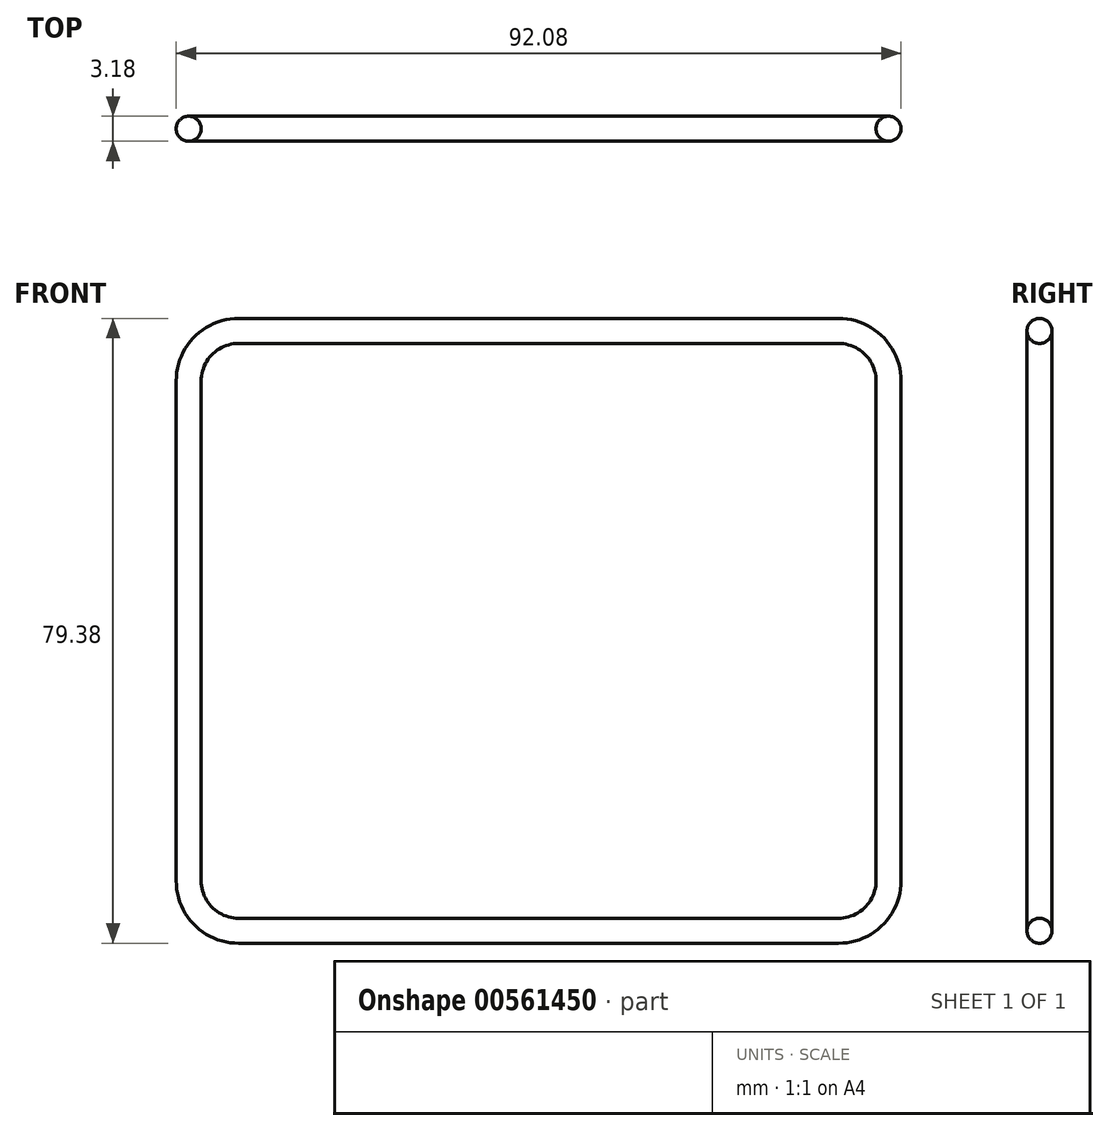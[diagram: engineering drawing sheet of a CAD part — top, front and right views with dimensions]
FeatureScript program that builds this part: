
annotation { "Feature Type Name" : "Feature", "Feature Type Description" : "" }
export const myFeature = defineFeature(function(context is Context, id is Id, definition is map)
    precondition{}
    {
        {
            var Q0;
            Q0=qCreatedBy(makeId("Front.planeOp"),FACE);
            var sketch = newSketch(context, id + "F0", { "sketchPlane" : qUnion([Q0])});
            skLineSegment(sketch, "E0.bottom", {"start": v(38.1, 38.1) * mm, "end": v(0, 38.1) * mm});
            skLineSegment(sketch, "E0.top", {"start": v(38.1, -38.1) * mm, "end": v(-38.1, -38.1) * mm});
            skLineSegment(sketch, "E0.left", {"start": v(44.45, 31.75) * mm, "end": v(44.45, -31.75) * mm});
            skLineSegment(sketch, "E0.right", {"start": v(-44.45, 31.75) * mm, "end": v(-44.45, -31.75) * mm});
            skPoint(sketch, "E0.middle", {"position": v(0, 0) * mm});
            skPoint(sketch, "E1.visualSharp", {"position": v(-44.45, 38.1) * mm});
            skArc(sketch, "E1.filletArc", {"start": v(-38.1, 38.1) * mm, "mid": v(-42.6, 36.24) * mm, "end": v(-44.45, 31.75) * mm});
            skPoint(sketch, "E2.visualSharp", {"position": v(44.45, 38.1) * mm});
            skArc(sketch, "E2.filletArc", {"start": v(44.45, 31.75) * mm, "mid": v(42.6, 36.24) * mm, "end": v(38.1, 38.1) * mm});
            skPoint(sketch, "E3.visualSharp", {"position": v(44.45, -38.1) * mm});
            skArc(sketch, "E3.filletArc", {"start": v(38.1, -38.1) * mm, "mid": v(42.6, -36.24) * mm, "end": v(44.45, -31.75) * mm});
            skPoint(sketch, "E4.visualSharp", {"position": v(-44.45, -38.1) * mm});
            skArc(sketch, "E4.filletArc", {"start": v(-44.45, -31.75) * mm, "mid": v(-42.6, -36.24) * mm, "end": v(-38.1, -38.1) * mm});
            skLineSegment(sketch, "E5", {"start": v(0, 38.1) * mm, "end": v(-38.1, 38.1) * mm});
            skSolve(sketch);
        }
        {
            var Q0;
            Q0=qCreatedBy(makeId("Right.planeOp"),FACE);
            var sketch = newSketch(context, id + "F1", { "sketchPlane" : qUnion([Q0])});
            skCircle(sketch, "E6", {"center": v(0, 38.1) * mm, "radius": 1.59 * mm});
            skSolve(sketch);
        }
        {
            var Q0;
            Q0=makeQuery(id+"F1.imprint","IMPRINT",FACE,{"disambiguationData":[TD([[makeQuery(id+"F1.imprint","IMPRINT",EDGE,{"derivedFrom":sQuery(id+"F1.wireOp",EDGE,"E6")}),1.0]])]});
            var Q1;
            Q1=sQuery(id+"F0.wireOp",EDGE,"E5");
            var Q2;
            Q2=sQuery(id+"F0.wireOp",EDGE,"E1.filletArc");
            var Q3;
            Q3=sQuery(id+"F0.wireOp",EDGE,"E0.right");
            var Q4;
            Q4=sQuery(id+"F0.wireOp",EDGE,"E4.filletArc");
            var Q5;
            Q5=sQuery(id+"F0.wireOp",EDGE,"E0.top");
            var Q6;
            Q6=sQuery(id+"F0.wireOp",EDGE,"E3.filletArc");
            var Q7;
            Q7=sQuery(id+"F0.wireOp",EDGE,"E0.left");
            var Q8;
            Q8=sQuery(id+"F0.wireOp",EDGE,"E2.filletArc");
            var Q9;
            Q9=sQuery(id+"F0.wireOp",EDGE,"E0.bottom");
            sweep(context, id + "F2", {"profiles" : qUnion([Q0]), "path" : qUnion([Q1, Q2, Q3, Q4, Q5, Q6, Q7, Q8, Q9])});
        }
    });
